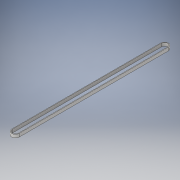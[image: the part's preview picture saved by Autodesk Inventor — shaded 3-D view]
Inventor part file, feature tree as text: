
AUTODESK INVENTOR PART (.ipt)
format: ipt  version: 2019 (Build 230136000, 136)  size: 105,472 bytes
history: native  units: mm
features: extrude x1, sketch x1
ambient origin geometry x8: Origin, YZ Plane, XZ Plane, XY Plane, X Axis, Y Axis, Z Axis, Center Point
bodies: Solid1 (feature_tree)
feature tree (2):
  extrude  "Extrusion1"  Depth=15.0mm
  sketch  "Sketch1"  dims[d0=15.0mm d1=710.0mm d2=3.0mm d3=15.0mm d4=0.0mm]
